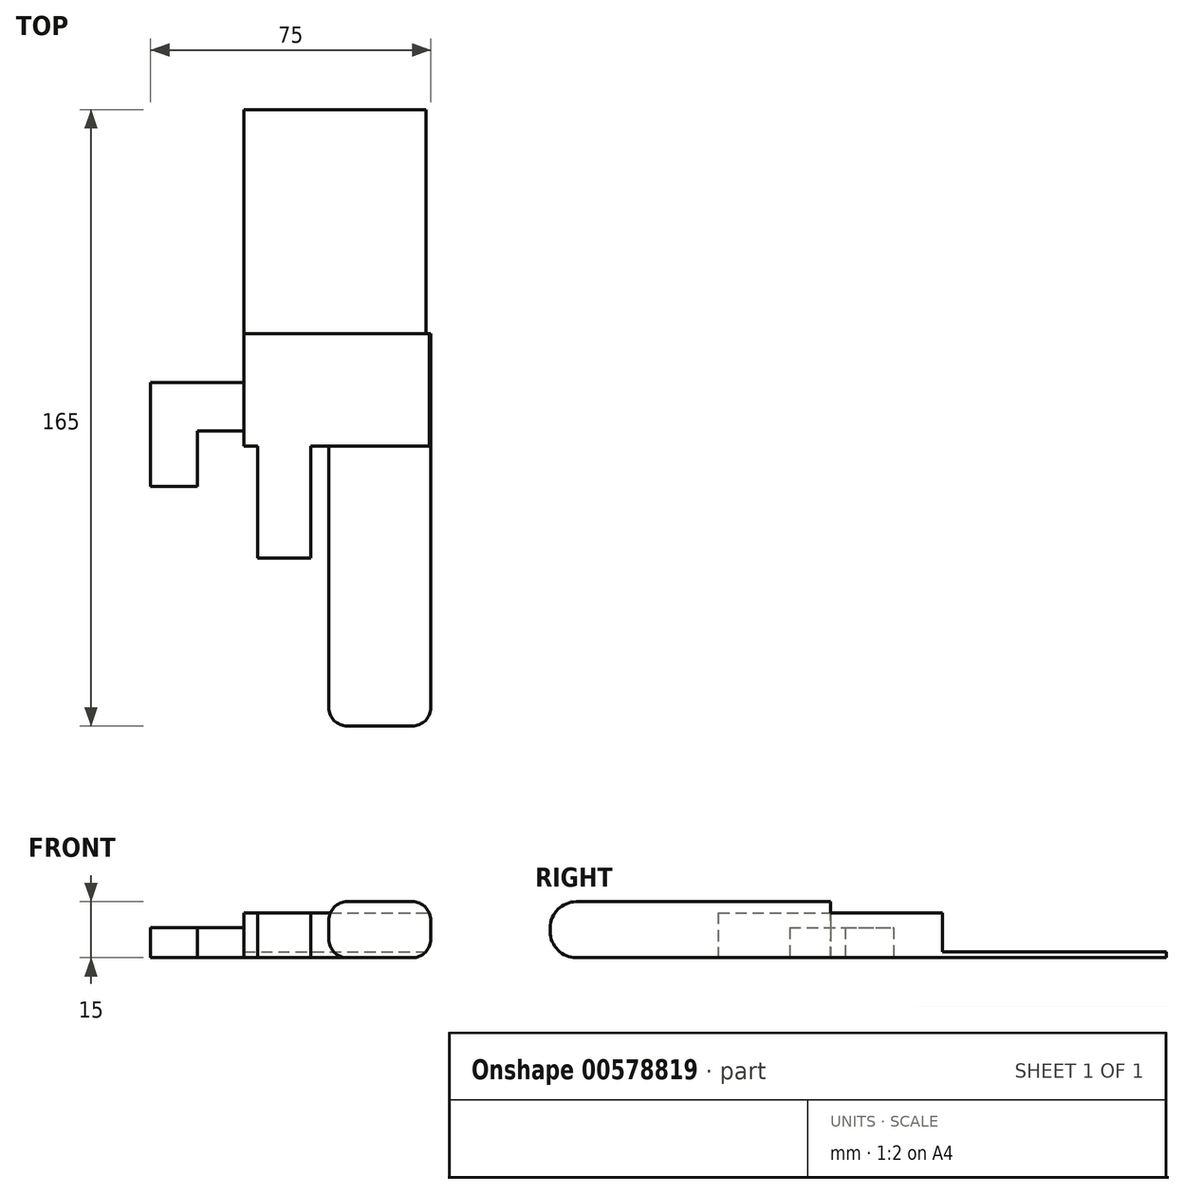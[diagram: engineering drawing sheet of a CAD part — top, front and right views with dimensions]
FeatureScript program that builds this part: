
annotation { "Feature Type Name" : "Feature", "Feature Type Description" : "" }
export const myFeature = defineFeature(function(context is Context, id is Id, definition is map)
    precondition{}
    {
        {
            var Q0;
            Q0=qCreatedBy(makeId("Top.planeOp"),FACE);
            var sketch = newSketch(context, id + "F0", { "sketchPlane" : qUnion([Q0])});
            skLineSegment(sketch, "E0.bottom", {"start": v(-22.68, 55.9) * mm, "end": v(27.32, 55.9) * mm});
            skLineSegment(sketch, "E0.top", {"start": v(-22.68, -34.1) * mm, "end": v(27.32, -34.1) * mm});
            skLineSegment(sketch, "E0.left", {"start": v(-22.68, 55.9) * mm, "end": v(-22.68, -34.1) * mm});
            skLineSegment(sketch, "E0.right", {"start": v(27.32, 55.9) * mm, "end": v(27.32, -34.1) * mm});
            skSolve(sketch);
        }
        {
            var Q0;
            Q0=makeQuery(id+"F0.imprint","IMPRINT",FACE,{"disambiguationData":[TD([[makeQuery(id+"F0.imprint","IMPRINT",EDGE,{"derivedFrom":sQuery(id+"F0.wireOp",EDGE,"E0.bottom")}),-1.0]])]});
            extrude(context, id + "F1", {"entities" : qUnion([Q0]), "depth" : 1.6 * mm, "offsetDistance" : 25 * mm});
        }
        {
            var Q0;
            Q0=makeQuery(id+"F1.opExtrude","CAP_FACE",FACE,{"disambiguationData":[OSD([sQuery(id+"F0.wireOp",EDGE,"E0.bottom"),sQuery(id+"F0.wireOp",EDGE,"E0.top"),sQuery(id+"F0.wireOp",EDGE,"E0.left"),sQuery(id+"F0.wireOp",EDGE,"E0.right")])],"isStart":false});
            var sketch = newSketch(context, id + "F2", { "sketchPlane" : qUnion([Q0])});
            skLineSegment(sketch, "E1.bottom", {"start": v(-22.68, -4.1) * mm, "end": v(27.32, -4.1) * mm});
            skLineSegment(sketch, "E1.top", {"start": v(-22.68, -34.1) * mm, "end": v(27.32, -34.1) * mm});
            skLineSegment(sketch, "E1.left", {"start": v(-22.68, -4.1) * mm, "end": v(-22.68, -34.1) * mm});
            skLineSegment(sketch, "E1.right", {"start": v(27.32, -4.1) * mm, "end": v(27.32, -34.1) * mm});
            skSolve(sketch);
        }
        {
            var Q0;
            Q0=makeQuery(id+"F2.imprint","IMPRINT",FACE,{"disambiguationData":[TD([[makeQuery(id+"F2.imprint","IMPRINT",EDGE,{"derivedFrom":sQuery(id+"F2.wireOp",EDGE,"E1.bottom")}),-1.0]])]});
            extrude(context, id + "F3", {"entities" : qUnion([Q0]), "operationType" : NewBodyOperationType.ADD, "depth" : 10.4 * mm, "offsetDistance" : 25 * mm});
        }
        {
            var Q0;
            Q0=makeQuery(id+"F3.boolean.opBoolean","MERGE",FACE,{"derivedFrom":[makeQuery(id+"F1.opExtrude","SWEPT_FACE",FACE,{"disambiguationData":[OSD([sQuery(id+"F0.wireOp",EDGE,"E0.left")])]}),makeQuery(id+"F3.opExtrude","SWEPT_FACE",FACE,{"disambiguationData":[OSD([sQuery(id+"F2.wireOp",EDGE,"E1.left")])]})]});
            var sketch = newSketch(context, id + "F4", { "sketchPlane" : qUnion([Q0])});
            skPoint(sketch, "E2.firstSnap0", {"position": v(30.1, 12) * mm});
            skLineSegment(sketch, "E2.bottom", {"start": v(30.1, 8) * mm, "end": v(17.1, 8) * mm});
            skLineSegment(sketch, "E2.top", {"start": v(30.1, 0) * mm, "end": v(17.1, 0) * mm});
            skLineSegment(sketch, "E2.left", {"start": v(30.1, 8) * mm, "end": v(30.1, 0) * mm});
            skLineSegment(sketch, "E2.right", {"start": v(17.1, 8) * mm, "end": v(17.1, 0) * mm});
            skSolve(sketch);
        }
        {
            var Q0;
            Q0=makeQuery(id+"F4.imprint","IMPRINT",FACE,{"disambiguationData":[TD([[makeQuery(id+"F4.imprint","IMPRINT",EDGE,{"derivedFrom":sQuery(id+"F4.wireOp",EDGE,"E2.bottom")}),1.0]])]});
            extrude(context, id + "F5", {"entities" : qUnion([Q0]), "operationType" : NewBodyOperationType.ADD, "depth" : 25 * mm, "offsetDistance" : 25 * mm});
        }
        {
            var Q0;
            Q0=makeQuery(id+"F5.opExtrude","SWEPT_FACE",FACE,{"disambiguationData":[OSD([sQuery(id+"F4.wireOp",EDGE,"E2.left")])]});
            var sketch = newSketch(context, id + "F6", { "sketchPlane" : qUnion([Q0])});
            skLineSegment(sketch, "E3.bottom", {"start": v(-47.68, 8) * mm, "end": v(-35.18, 8) * mm});
            skLineSegment(sketch, "E3.top", {"start": v(-47.68, 0) * mm, "end": v(-35.18, 0) * mm});
            skLineSegment(sketch, "E3.left", {"start": v(-35.18, 8) * mm, "end": v(-35.18, 0) * mm});
            skLineSegment(sketch, "E3.right", {"start": v(-47.68, 8) * mm, "end": v(-47.68, 0) * mm});
            skSolve(sketch);
        }
        {
            var Q0;
            Q0=makeQuery(id+"F6.imprint","IMPRINT",FACE,{"disambiguationData":[TD([[makeQuery(id+"F6.imprint","IMPRINT",EDGE,{"derivedFrom":sQuery(id+"F6.wireOp",EDGE,"E3.bottom")}),-1.0]])]});
            extrude(context, id + "F7", {"entities" : qUnion([Q0]), "operationType" : NewBodyOperationType.ADD, "depth" : 14.9 * mm, "offsetDistance" : 25 * mm});
        }
        {
            var Q0;
            Q0=qCreatedBy(makeId("Top.planeOp"),FACE);
            var sketch = newSketch(context, id + "F8", { "sketchPlane" : qUnion([Q0])});
            skLineSegment(sketch, "E4.bottom", {"start": v(0, -34.1) * mm, "end": v(27.32, -34.1) * mm});
            skLineSegment(sketch, "E4.top", {"start": v(0, -109.1) * mm, "end": v(27.32, -109.1) * mm});
            skLineSegment(sketch, "E4.left", {"start": v(0, -34.1) * mm, "end": v(0, -109.1) * mm});
            skLineSegment(sketch, "E4.right", {"start": v(27.32, -34.1) * mm, "end": v(27.32, -109.1) * mm});
            skSolve(sketch);
        }
        {
            var Q0;
            Q0=makeQuery(id+"F8.imprint","IMPRINT",FACE,{"disambiguationData":[TD([[makeQuery(id+"F8.imprint","IMPRINT",EDGE,{"derivedFrom":sQuery(id+"F8.wireOp",EDGE,"E4.bottom")}),-1.0]])]});
            extrude(context, id + "F9", {"entities" : qUnion([Q0]), "operationType" : NewBodyOperationType.ADD, "depth" : 15 * mm, "offsetDistance" : 25 * mm});
        }
        {
            var Q0;
            Q0=makeQuery(id+"F9.opExtrude","CAP_EDGE",EDGE,{"disambiguationData":[OSD([sQuery(id+"F8.wireOp",EDGE,"E4.right")])],"isStart":false});
            var Q1;
            Q1=makeQuery(id+"F9.opExtrude","CAP_EDGE",EDGE,{"disambiguationData":[OSD([sQuery(id+"F8.wireOp",EDGE,"E4.right")])],"isStart":true});
            var Q2;
            Q2=makeQuery(id+"F9.opExtrude","CAP_EDGE",EDGE,{"disambiguationData":[OSD([sQuery(id+"F8.wireOp",EDGE,"E4.left")])],"isStart":false});
            var Q3;
            Q3=makeQuery(id+"F9.opExtrude","CAP_EDGE",EDGE,{"disambiguationData":[OSD([sQuery(id+"F8.wireOp",EDGE,"E4.left")])],"isStart":true});
            var Q4;
            Q4=makeQuery(id+"F9.opExtrude","SWEPT_EDGE",EDGE,{"disambiguationData":[OSD([sQuery(id+"F8.wireOp",EDGE,"E4.top"),sQuery(id+"F8.wireOp",EDGE,"E4.left")])]});
            var Q5;
            Q5=makeQuery(id+"F9.opExtrude","SWEPT_EDGE",EDGE,{"disambiguationData":[OSD([sQuery(id+"F8.wireOp",EDGE,"E4.top"),sQuery(id+"F8.wireOp",EDGE,"E4.right")])]});
            fillet(context, id + "F10", {"entities" : qUnion([Q0, Q1, Q2, Q3, Q4, Q5]), "radius" : 5 * mm, "tangentPropagation" : true, "allowEdgeOverflow" : false});
        }
        {
            var Q0;
            Q0=makeQuery(id+"F9.opExtrude","CAP_EDGE",EDGE,{"disambiguationData":[OSD([sQuery(id+"F8.wireOp",EDGE,"E4.top")])],"isStart":true});
            var Q1;
            Q1=makeQuery(id+"F9.opExtrude","CAP_EDGE",EDGE,{"disambiguationData":[OSD([sQuery(id+"F8.wireOp",EDGE,"E4.top")])],"isStart":false});
            fillet(context, id + "F11", {"entities" : qUnion([Q0, Q1]), "radius" : 7 * mm, "tangentPropagation" : true, "allowEdgeOverflow" : false});
        }
        {
            var Q0;
            Q0=makeQuery(id+"F3.boolean.opBoolean","MERGE",FACE,{"derivedFrom":[makeQuery(id+"F1.opExtrude","SWEPT_FACE",FACE,{"disambiguationData":[OSD([sQuery(id+"F0.wireOp",EDGE,"E0.top")])]}),makeQuery(id+"F3.opExtrude","SWEPT_FACE",FACE,{"disambiguationData":[OSD([sQuery(id+"F2.wireOp",EDGE,"E1.top")])]})]});
            var sketch = newSketch(context, id + "F12", { "sketchPlane" : qUnion([Q0])});
            skLineSegment(sketch, "E5.bottom", {"start": v(-19.06, 12) * mm, "end": v(-4.81, 12) * mm});
            skLineSegment(sketch, "E5.top", {"start": v(-19.06, 0) * mm, "end": v(-4.81, 0) * mm});
            skLineSegment(sketch, "E5.left", {"start": v(-19.06, 12) * mm, "end": v(-19.06, 0) * mm});
            skLineSegment(sketch, "E5.right", {"start": v(-4.81, 12) * mm, "end": v(-4.81, 0) * mm});
            skSolve(sketch);
        }
        {
            var Q0;
            Q0=makeQuery(id+"F12.imprint","IMPRINT",FACE,{"disambiguationData":[TD([[makeQuery(id+"F12.imprint","IMPRINT",EDGE,{"derivedFrom":sQuery(id+"F12.wireOp",EDGE,"E5.bottom")}),-1.0]])]});
            extrude(context, id + "F13", {"entities" : qUnion([Q0]), "operationType" : NewBodyOperationType.ADD, "depth" : 30 * mm, "offsetDistance" : 25 * mm});
        }
    });
